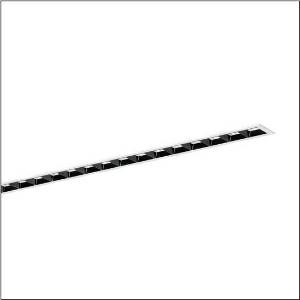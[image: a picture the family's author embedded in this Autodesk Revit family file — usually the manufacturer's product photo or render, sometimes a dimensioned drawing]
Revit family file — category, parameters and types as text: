
# Revit family: silica_21_51mx11da34wb
name_source: partatom
category: Lighting Fixtures
units: mm (PartAtom-declared; Revit-internal decimal feet)

## family parameters
Cut with Voids When Loaded = No
Host = Face
Light Source = No
Part Type = Normal
Room Calculation Point = No
Round Connector Dimension = Use Diameter
Shared = No

## types (1)
- --- (1 x LED, 4320 lm, 27.4 W, 3000K)
    Apparent Load = 27 VA
    CIE Flux Codes = 87 99 100 100 100
    Color Rendering = 80
    Color Temperature = 3000K
    Default Elevation = 1800 mm
    Description = Silica 21, office luminaire, primary light control with darklight reflector, of PMMA, black, CAT 2 (L<= 3000cd/m²), light emission: direct distribution, primary light characteristic: symmetric, installation type: recessed, LED, rated luminous flux: 4.320lm, luminous efficacy: 158lm/W, light colour: 830, colour temperature: 3000K, control gear: DALI 2, with terminal, 3+2-pole, max. 2.5mm², mains connection: 220..240V, AC, 50/60Hz, rated input power: 27.4W, luminaire housing, of aluminium, traffic white (RAL 9016), length: 1.228mm, width: 79mm, height: 53mm, protection rating (complete): IP20, insulation class (complete): insulation class I (protective earthing), certification: CE, ENEC, VDE, permissible operating ambient temperature: 0..+35°C, standard: EN 50419, packaging unit: 1 piece
    Height = 0 mm  [stored 0 ft]
    Lamp = 1 x LED
    Lamp Light Flux = 4320 lm
    Lamp Power = 27.4 W
    Lamp count = 1
    Length = 1227 mm
    Luminous efficacy = 158 lm/W
    Manufacturer = Siteco
    ModVariant = No
    Model = 51MX11DA34WB
    Mounting Place = Ceiling
    Mounting Type = Recessed
    Number of Poles = 1
    OnlyDefault = Yes
    Power Factor = 1
    Product Name = Silica 21
    Product group = office luminaire | ceiling recessed
    ProductGroupID = 400
    Protection Class = Protection class I
    Protection Degree = IP 20
    RLX_Detail_Level = 1
    RLX_Emergency_Light_Flux = 0 lm
    RLX_Emergency_Type = 0
    RLX_Emergency_Type_DB = No
    RlxData = <blob elided: 39197 chars, md5=4f0565e3>
    Socket = socket
    Standby Power = 0 W
    System Light Flux = 4320 lm
    System Power = 27 W
    Type Comments = factory setting: luminous flux: 100 % | dim-lin: 254 | 393 mA
    Type Image = l_1335880.jpg
    URL = http://relux.com
    VarID = @adj_028329
    Voltage = 0 V
    Weight = 0.00 kg
    Width = 79 mm

note: [stored X ft] marks values corroborated as IEEE doubles in the binary element streams (Revit-internal decimal feet)

## geometry (parser evidence)
native form markers: Blend x4, Sweep x9
no freeform markers — native parametric forms only
